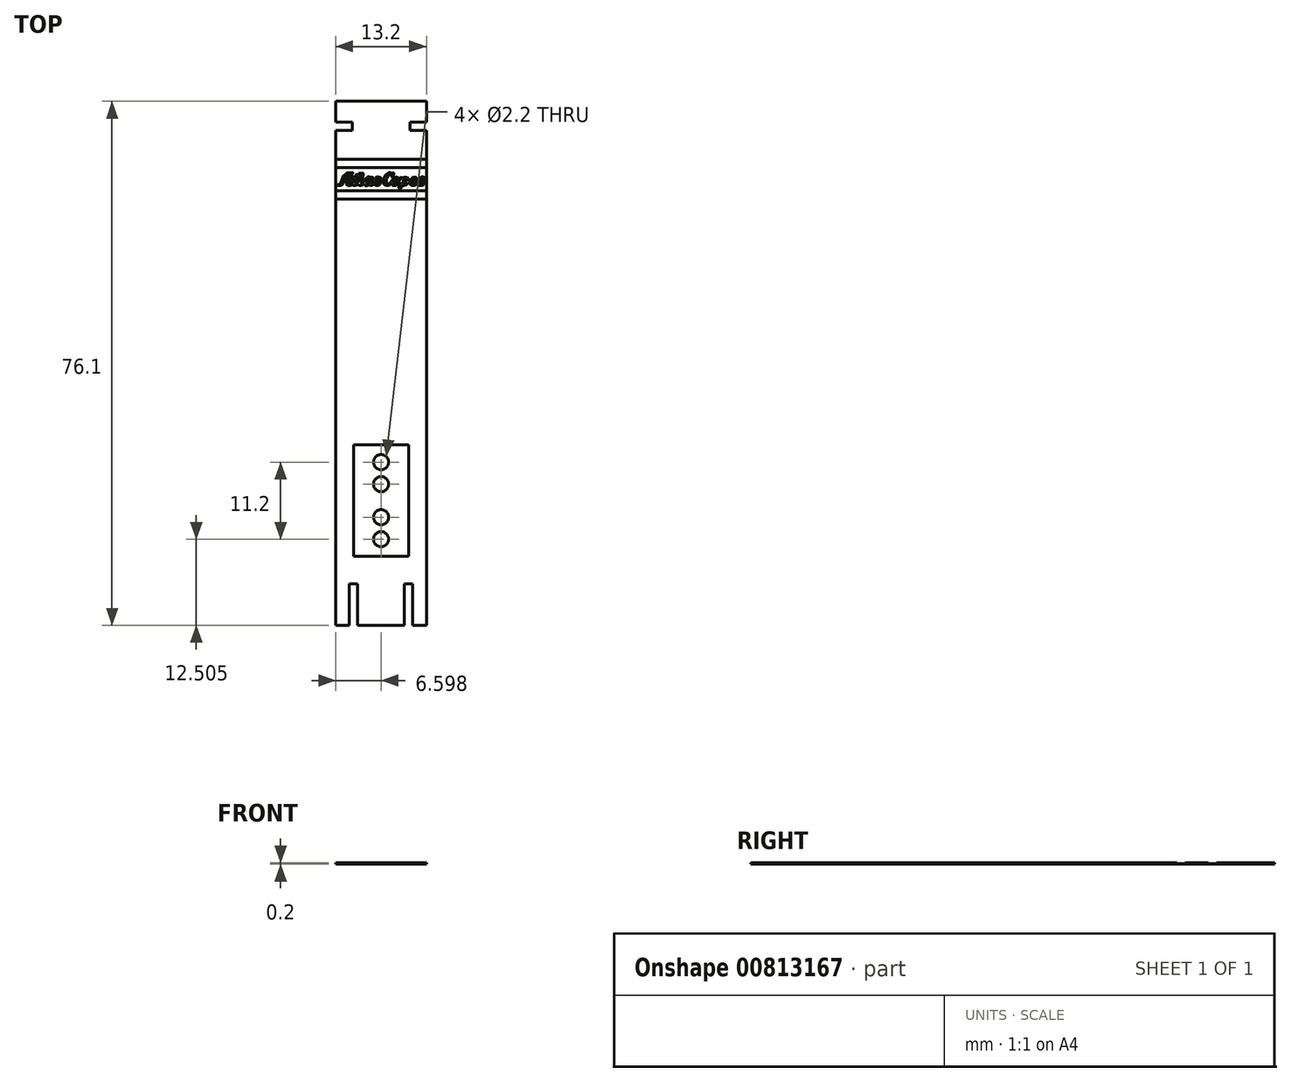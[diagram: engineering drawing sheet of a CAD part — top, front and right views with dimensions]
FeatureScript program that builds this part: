
annotation { "Feature Type Name" : "Feature", "Feature Type Description" : "" }
export const myFeature = defineFeature(function(context is Context, id is Id, definition is map)
    precondition{}
    {
        {
            var Q0;
            Q0=qCreatedBy(makeId("Top.planeOp"),FACE);
            var sketch = newSketch(context, id + "F0", { "sketchPlane" : qUnion([Q0])});
            skLineSegment(sketch, "E0.bottom", {"start": v(-6.48, 59.58) * mm, "end": v(6.72, 59.58) * mm});
            skLineSegment(sketch, "E0.top", {"start": v(-6.48, -16.52) * mm, "end": v(6.72, -16.52) * mm});
            skLineSegment(sketch, "E0.left", {"start": v(-6.48, 59.58) * mm, "end": v(-6.48, -16.52) * mm});
            skLineSegment(sketch, "E0.right", {"start": v(6.72, 59.58) * mm, "end": v(6.72, -16.52) * mm});
            skSolve(sketch);
        }
        {
            var Q0;
            Q0=makeQuery(id+"F0.imprint","IMPRINT",FACE,{"disambiguationData":[TD([[makeQuery(id+"F0.imprint","IMPRINT",EDGE,{"derivedFrom":sQuery(id+"F0.wireOp",EDGE,"E0.bottom")}),-1.0]])]});
            extrude(context, id + "F1", {"entities" : qUnion([Q0]), "depth" : 0.2 * mm, "offsetDistance" : 25 * mm});
        }
        {
            var Q0;
            Q0=makeQuery(id+"F1.opExtrude","CAP_FACE",FACE,{"disambiguationData":[OSD([sQuery(id+"F0.wireOp",EDGE,"E0.bottom"),sQuery(id+"F0.wireOp",EDGE,"E0.top"),sQuery(id+"F0.wireOp",EDGE,"E0.left"),sQuery(id+"F0.wireOp",EDGE,"E0.right")])],"isStart":false});
            var sketch = newSketch(context, id + "F2", { "sketchPlane" : qUnion([Q0])});
            skLineSegment(sketch, "E1", {"start": v(6.72, 56.58) * mm, "end": v(4.32, 56.58) * mm});
            skLineSegment(sketch, "E2", {"start": v(4.32, 56.58) * mm, "end": v(4.32, 55.38) * mm});
            skLineSegment(sketch, "E3", {"start": v(4.32, 55.38) * mm, "end": v(6.72, 55.38) * mm});
            skLineSegment(sketch, "E4", {"start": v(6.72, 55.38) * mm, "end": v(6.72, 56.58) * mm});
            skLineSegment(sketch, "E5", {"start": v(-6.48, 56.58) * mm, "end": v(-4.08, 56.58) * mm});
            skLineSegment(sketch, "E6", {"start": v(-4.08, 56.58) * mm, "end": v(-4.08, 55.38) * mm});
            skLineSegment(sketch, "E7", {"start": v(-4.08, 55.38) * mm, "end": v(-6.48, 55.38) * mm});
            skLineSegment(sketch, "E8", {"start": v(-6.48, 55.38) * mm, "end": v(-6.48, 56.58) * mm});
            skSolve(sketch);
        }
        {
            var Q0;
            Q0=makeQuery(id+"F2.imprint","IMPRINT",FACE,{"disambiguationData":[TD([[makeQuery(id+"F2.imprint","IMPRINT",EDGE,{"derivedFrom":sQuery(id+"F2.wireOp",EDGE,"E5")}),-1.0]])]});
            var Q1;
            Q1=makeQuery(id+"F2.imprint","IMPRINT",FACE,{"disambiguationData":[TD([[makeQuery(id+"F2.imprint","IMPRINT",EDGE,{"derivedFrom":sQuery(id+"F2.wireOp",EDGE,"E1")}),1.0]])]});
            extrude(context, id + "F3", {"entities" : qUnion([Q0, Q1]), "operationType" : NewBodyOperationType.REMOVE, "oppositeDirection" : true, "depth" : 0.2 * mm, "offsetDistance" : 25 * mm});
        }
        {
            var Q0;
            Q0=makeQuery(id+"F1.opExtrude","CAP_FACE",FACE,{"disambiguationData":[OSD([sQuery(id+"F0.wireOp",EDGE,"E0.bottom"),sQuery(id+"F0.wireOp",EDGE,"E0.top"),sQuery(id+"F0.wireOp",EDGE,"E0.left"),sQuery(id+"F0.wireOp",EDGE,"E0.right")])],"isStart":false});
            var sketch = newSketch(context, id + "F4", { "sketchPlane" : qUnion([Q0])});
            skLineSegment(sketch, "E9", {"start": v(6.72, 51.18) * mm, "end": v(-6.48, 51.18) * mm});
            skLineSegment(sketch, "E10", {"start": v(-6.48, 51.18) * mm, "end": v(-6.48, 49.98) * mm});
            skLineSegment(sketch, "E11", {"start": v(-6.48, 49.98) * mm, "end": v(6.72, 49.98) * mm});
            skLineSegment(sketch, "E12", {"start": v(6.72, 49.98) * mm, "end": v(6.72, 51.18) * mm});
            skLineSegment(sketch, "E13", {"start": v(6.72, 46.58) * mm, "end": v(-6.48, 46.58) * mm});
            skLineSegment(sketch, "E14", {"start": v(-6.48, 46.58) * mm, "end": v(-6.48, 45.38) * mm});
            skLineSegment(sketch, "E15", {"start": v(-6.48, 45.38) * mm, "end": v(6.72, 45.38) * mm});
            skLineSegment(sketch, "E16", {"start": v(6.72, 45.38) * mm, "end": v(6.72, 46.58) * mm});
            skSolve(sketch);
        }
        {
            var Q0;
            Q0=makeQuery(id+"F4.imprint","IMPRINT",FACE,{"disambiguationData":[TD([[makeQuery(id+"F4.imprint","IMPRINT",EDGE,{"derivedFrom":sQuery(id+"F4.wireOp",EDGE,"E9")}),1.0]])]});
            var Q1;
            Q1=makeQuery(id+"F4.imprint","IMPRINT",FACE,{"disambiguationData":[TD([[makeQuery(id+"F4.imprint","IMPRINT",EDGE,{"derivedFrom":sQuery(id+"F4.wireOp",EDGE,"E13")}),1.0]])]});
            extrude(context, id + "F5", {"entities" : qUnion([Q0, Q1]), "operationType" : NewBodyOperationType.REMOVE, "oppositeDirection" : true, "depth" : 0.1 * mm, "offsetDistance" : 25 * mm});
        }
        {
            var Q0;
            {var subQ0=sQuery(id+"F0.wireOp",EDGE,"E0.left");var subQ1=sQuery(id+"F0.wireOp",EDGE,"E0.right");Q0=makeQuery(id+"F5.boolean.opBoolean","SPLIT",FACE,{"disambiguationData":[TD([makeQuery(id+"F5.opExtrude","SWEPT_FACE",FACE,{"disambiguationData":[OSD([sQuery(id+"F4.wireOp",EDGE,"E11")])]})])],"derivedFrom":makeQuery(id+"F1.opExtrude","CAP_FACE",FACE,{"disambiguationData":[OSD([sQuery(id+"F0.wireOp",EDGE,"E0.bottom"),sQuery(id+"F0.wireOp",EDGE,"E0.top"),subQ0,subQ1])],"isStart":false})});}
            var sketch = newSketch(context, id + "F6", { "sketchPlane" : qUnion([Q0])});
            skFitSpline(sketch, "E17", {"points": [v(-6.24, 47.53) * mm, v(-6.25, 47.34) * mm, v(-6.22, 47.33) * mm, v(-6.17, 47.33) * mm, v(-6.12, 47.32) * mm, v(-6.08, 47.32) * mm, v(-6.04, 47.33) * mm, v(-6, 47.32) * mm, v(-5.96, 47.33) * mm, v(-5.92, 47.33) * mm, v(-5.88, 47.34) * mm, v(-5.83, 47.35) * mm, v(-5.78, 47.36) * mm, v(-5.55, 47.5) * mm, v(-5.38, 47.67) * mm, v(-5.3, 47.83) * mm, v(-5.25, 47.98) * mm, v(-5.23, 48.04) * mm, v(-5.23, 48.05) * mm, v(-5.22, 48.07) * mm, v(-5.22, 48.1) * mm, v(-5.2, 48.13) * mm, v(-5.18, 48.16) * mm, v(-5.12, 48.17) * mm, v(-5.04, 48.17) * mm, v(-4.97, 48.17) * mm, v(-4.93, 48.17) * mm, v(-4.88, 48.17) * mm, v(-4.85, 48.17) * mm, v(-4.82, 48.17) * mm, v(-4.8, 48.17) * mm, v(-4.8, 48.17) * mm, v(-4.8, 48.13) * mm, v(-4.8, 48.1) * mm, v(-4.81, 48.03) * mm, v(-4.83, 47.97) * mm, v(-4.85, 47.91) * mm, v(-4.86, 47.87) * mm, v(-4.88, 47.81) * mm, v(-4.9, 47.75) * mm, v(-4.92, 47.7) * mm, v(-4.92, 47.55) * mm, v(-4.87, 47.44) * mm, v(-4.78, 47.36) * mm, v(-4.67, 47.32) * mm, v(-4.52, 47.32) * mm, v(-4.41, 47.33) * mm, v(-4.3, 47.37) * mm, v(-4.2, 47.43) * mm, v(-4.13, 47.48) * mm, v(-4.1, 47.51) * mm, v(-4.07, 47.55) * mm, v(-4.05, 47.56) * mm, v(-4.03, 47.52) * mm, v(-4.02, 47.46) * mm, v(-4.01, 47.42) * mm, v(-3.97, 47.4) * mm, v(-3.94, 47.36) * mm, v(-3.89, 47.34) * mm, v(-3.85, 47.33) * mm, v(-3.8, 47.32) * mm], "startDerivative": vector(-1.04, -8.47) * mm, "endDerivative": vector(3.3, -0.6) * mm});
            skFitSpline(sketch, "E18", {"points": [v(-3.8, 47.32) * mm, v(-3.7, 47.32) * mm, v(-3.55, 47.35) * mm, v(-3.45, 47.4) * mm, v(-3.4, 47.43) * mm, v(-3.34, 47.47) * mm, v(-3.3, 47.5) * mm, v(-3.27, 47.53) * mm, v(-3.24, 47.55) * mm, v(-3.2, 47.57) * mm, v(-3.18, 47.56) * mm, v(-3.17, 47.52) * mm, v(-3.14, 47.47) * mm, v(-3.13, 47.42) * mm, v(-3.1, 47.4) * mm, v(-3.06, 47.35) * mm, v(-3, 47.32) * mm, v(-2.94, 47.32) * mm, v(-2.89, 47.32) * mm, v(-2.84, 47.32) * mm, v(-2.8, 47.32) * mm, v(-2.75, 47.32) * mm, v(-2.72, 47.35) * mm, v(-2.69, 47.38) * mm, v(-2.64, 47.4) * mm, v(-2.61, 47.43) * mm, v(-2.58, 47.46) * mm, v(-2.44, 47.57) * mm, v(-2.41, 47.62) * mm, v(-2.39, 47.63) * mm, v(-2.34, 47.63) * mm, v(-2.34, 47.61) * mm, v(-2.34, 47.58) * mm, v(-2.33, 47.56) * mm, v(-2.32, 47.53) * mm, v(-2.25, 47.45) * mm, v(-2.17, 47.38) * mm, v(-2.13, 47.35) * mm, v(-2.06, 47.32) * mm, v(-1.98, 47.32) * mm, v(-1.92, 47.32) * mm, v(-1.83, 47.35) * mm, v(-1.75, 47.4) * mm, v(-1.7, 47.44) * mm, v(-1.66, 47.46) * mm, v(-1.64, 47.48) * mm, v(-1.62, 47.48) * mm, v(-1.6, 47.5) * mm, v(-1.6, 47.48) * mm, v(-1.59, 47.48) * mm, v(-1.57, 47.44) * mm, v(-1.55, 47.42) * mm, v(-1.52, 47.38) * mm, v(-1.5, 47.37) * mm, v(-1.48, 47.36) * mm, v(-1.45, 47.35) * mm], "startDerivative": vector(3.88, -0.24) * mm, "endDerivative": vector(2.21, -0.04) * mm});
            skFitSpline(sketch, "E19", {"points": [v(-1.45, 47.35) * mm, v(-1.4, 47.34) * mm, v(-1.35, 47.34) * mm, v(-1.29, 47.34) * mm, v(-1.22, 47.35) * mm, v(-1.17, 47.37) * mm, v(-1.13, 47.4) * mm, v(-1.1, 47.4) * mm, v(-1.07, 47.42) * mm, v(-1.03, 47.44) * mm, v(-1, 47.47) * mm, v(-0.98, 47.5) * mm, v(-0.97, 47.52) * mm, v(-0.95, 47.53) * mm, v(-0.93, 47.54) * mm, v(-0.9, 47.52) * mm, v(-0.88, 47.49) * mm, v(-0.84, 47.46) * mm, v(-0.8, 47.42) * mm, v(-0.77, 47.39) * mm, v(-0.71, 47.35) * mm, v(-0.67, 47.34) * mm, v(-0.6, 47.32) * mm, v(-0.53, 47.33) * mm, v(-0.47, 47.33) * mm, v(-0.4, 47.33) * mm, v(-0.34, 47.33) * mm, v(-0.3, 47.34) * mm, v(-0.23, 47.37) * mm, v(-0.16, 47.4) * mm, v(-0.13, 47.42) * mm, v(-0.05, 47.48) * mm, v(0.04, 47.6) * mm, v(0.07, 47.73) * mm, v(0.04, 47.89) * mm, v(-0.04, 47.98) * mm, v(-0.16, 48.06) * mm, v(-0.3, 48.14) * mm, v(-0.37, 48.22) * mm, v(-0.4, 48.27) * mm, v(-0.4, 48.34) * mm, v(-0.34, 48.43) * mm, v(-0.3, 48.45) * mm, v(-0.23, 48.46) * mm, v(-0.16, 48.45) * mm, v(-0.14, 48.44) * mm, v(-0.14, 48.39) * mm, v(-0.17, 48.37) * mm, v(-0.18, 48.33) * mm, v(-0.18, 48.3) * mm, v(-0.15, 48.25) * mm, v(-0.13, 48.21) * mm, v(-0.07, 48.17) * mm, v(0, 48.16) * mm, v(0.03, 48.17) * mm, v(0.1, 48.2) * mm, v(0.13, 48.24) * mm, v(0.15, 48.3) * mm, v(0.11, 48.43) * mm, v(0.05, 48.53) * mm, v(-0.04, 48.59) * mm, v(-0.15, 48.63) * mm, v(-0.27, 48.64) * mm, v(-0.4, 48.62) * mm, v(-0.48, 48.6) * mm, v(-0.57, 48.54) * mm, v(-0.66, 48.45) * mm, v(-0.72, 48.36) * mm, v(-0.74, 48.27) * mm, v(-0.74, 48.18) * mm, v(-0.73, 48.08) * mm, v(-0.65, 47.98) * mm, v(-0.6, 47.94) * mm, v(-0.52, 47.88) * mm, v(-0.44, 47.82) * mm, v(-0.37, 47.77) * mm, v(-0.35, 47.68) * mm, v(-0.35, 47.6) * mm, v(-0.39, 47.56) * mm, v(-0.42, 47.53) * mm, v(-0.47, 47.5) * mm, v(-0.5, 47.49) * mm, v(-0.57, 47.46) * mm, v(-0.63, 47.49) * mm, v(-0.68, 47.5) * mm, v(-0.72, 47.55) * mm, v(-0.75, 47.57) * mm, v(-0.76, 47.6) * mm, v(-0.73, 47.63) * mm, v(-0.68, 47.66) * mm, v(-0.65, 47.76) * mm, v(-0.66, 47.84) * mm, v(-0.72, 47.9) * mm, v(-0.8, 47.9) * mm, v(-0.89, 47.9) * mm, v(-0.92, 47.85) * mm, v(-0.96, 47.82) * mm, v(-0.95, 47.74) * mm, v(-0.96, 47.68) * mm, v(-1.01, 47.63) * mm, v(-1.05, 47.6) * mm, v(-1.1, 47.6) * mm], "startDerivative": vector(4.9, -2.39) * mm, "endDerivative": vector(-5.28, -0.79) * mm});
            skFitSpline(sketch, "E20", {"points": [v(-1.1, 47.6) * mm, v(-1.15, 47.6) * mm, v(-1.2, 47.6) * mm, v(-1.22, 47.63) * mm, v(-1.21, 47.72) * mm, v(-1.18, 47.85) * mm, v(-1.14, 48.04) * mm, v(-1.1, 48.25) * mm, v(-1.06, 48.34) * mm, v(-1.04, 48.43) * mm, v(-1.02, 48.52) * mm, v(-1, 48.57) * mm, v(-1.07, 48.58) * mm, v(-1.14, 48.58) * mm, v(-1.22, 48.58) * mm, v(-1.33, 48.58) * mm, v(-1.38, 48.58) * mm, v(-1.38, 48.5) * mm, v(-1.38, 48.5) * mm, v(-1.42, 48.5) * mm, v(-1.45, 48.54) * mm, v(-1.49, 48.56) * mm, v(-1.55, 48.6) * mm, v(-1.63, 48.62) * mm, v(-1.7, 48.63) * mm, v(-1.75, 48.61) * mm, v(-1.81, 48.6) * mm, v(-1.87, 48.57) * mm, v(-1.91, 48.54) * mm, v(-1.96, 48.5) * mm, v(-2.05, 48.44) * mm, v(-2.13, 48.34) * mm, v(-2.2, 48.26) * mm, v(-2.25, 48.2) * mm, v(-2.28, 48.13) * mm, v(-2.37, 47.98) * mm, v(-2.4, 47.9) * mm, v(-2.44, 47.86) * mm, v(-2.47, 47.8) * mm, v(-2.52, 47.73) * mm, v(-2.6, 47.65) * mm, v(-2.61, 47.62) * mm, v(-2.64, 47.6) * mm, v(-2.67, 47.6) * mm, v(-2.7, 47.6) * mm, v(-2.71, 47.61) * mm, v(-2.73, 47.62) * mm, v(-2.75, 47.63) * mm, v(-2.75, 47.64) * mm, v(-2.76, 47.66) * mm, v(-2.75, 47.72) * mm, v(-2.73, 47.8) * mm, v(-2.71, 47.89) * mm, v(-2.69, 47.97) * mm, v(-2.65, 48.1) * mm, v(-2.63, 48.18) * mm, v(-2.61, 48.32) * mm, v(-2.58, 48.48) * mm, v(-2.53, 48.65) * mm, v(-2.49, 48.77) * mm, v(-2.45, 48.9) * mm, v(-2.43, 49) * mm, v(-2.42, 49.1) * mm, v(-2.42, 49.13) * mm, v(-2.44, 49.14) * mm, v(-2.48, 49.13) * mm, v(-2.5, 49.13) * mm, v(-2.68, 49.14) * mm, v(-2.78, 49.14) * mm, v(-2.92, 49.14) * mm, v(-3.03, 49.15) * mm, v(-3.07, 49.15) * mm, v(-3.07, 49.12) * mm, v(-3.08, 49.05) * mm, v(-3.09, 49) * mm, v(-3.07, 48.97) * mm, v(-3.03, 48.96) * mm, v(-2.97, 48.97) * mm, v(-2.93, 48.97) * mm, v(-2.89, 48.97) * mm, v(-2.87, 48.97) * mm, v(-2.88, 48.9) * mm, v(-2.9, 48.81) * mm, v(-2.9, 48.75) * mm, v(-2.93, 48.65) * mm], "startDerivative": vector(-5.04, 0.24) * mm, "endDerivative": vector(-1.95, -7.23) * mm});
            skFitSpline(sketch, "E21", {"points": [v(-2.93, 48.65) * mm, v(-2.96, 48.52) * mm, v(-2.97, 48.43) * mm, v(-3, 48.3) * mm, v(-3.02, 48.23) * mm, v(-3.05, 48.16) * mm, v(-3.07, 48.06) * mm, v(-3.1, 48) * mm, v(-3.13, 47.9) * mm, v(-3.17, 47.82) * mm, v(-3.23, 47.76) * mm, v(-3.28, 47.7) * mm, v(-3.35, 47.66) * mm, v(-3.41, 47.63) * mm, v(-3.45, 47.6) * mm, v(-3.5, 47.6) * mm, v(-3.55, 47.6) * mm, v(-3.6, 47.61) * mm, v(-3.62, 47.62) * mm, v(-3.64, 47.67) * mm, v(-3.63, 47.75) * mm, v(-3.62, 47.84) * mm, v(-3.6, 47.93) * mm, v(-3.57, 48.08) * mm, v(-3.53, 48.22) * mm, v(-3.51, 48.32) * mm, v(-3.5, 48.4) * mm, v(-3.48, 48.44) * mm, v(-3.42, 48.44) * mm, v(-3.3, 48.44) * mm, v(-3.2, 48.44) * mm, v(-3.19, 48.44) * mm, v(-3.18, 48.48) * mm, v(-3.18, 48.54) * mm, v(-3.18, 48.57) * mm, v(-3.23, 48.57) * mm, v(-3.3, 48.57) * mm, v(-3.39, 48.56) * mm, v(-3.42, 48.57) * mm, v(-3.43, 48.62) * mm, v(-3.41, 48.65) * mm, v(-3.4, 48.7) * mm, v(-3.38, 48.75) * mm, v(-3.36, 48.84) * mm, v(-3.35, 48.9) * mm, v(-3.34, 48.95) * mm, v(-3.34, 48.96) * mm, v(-3.4, 48.97) * mm, v(-3.42, 48.97) * mm, v(-3.49, 48.98) * mm, v(-3.5, 48.96) * mm, v(-3.5, 48.93) * mm, v(-3.55, 48.88) * mm, v(-3.56, 48.85) * mm, v(-3.58, 48.8) * mm, v(-3.62, 48.77) * mm, v(-3.64, 48.75) * mm, v(-3.67, 48.72) * mm, v(-3.7, 48.69) * mm, v(-3.71, 48.68) * mm, v(-3.75, 48.65) * mm, v(-3.79, 48.61) * mm, v(-3.82, 48.59) * mm, v(-3.88, 48.59) * mm, v(-3.92, 48.59) * mm, v(-3.96, 48.59) * mm, v(-4.01, 48.59) * mm, v(-4.05, 48.59) * mm, v(-4.07, 48.53) * mm, v(-4.06, 48.5) * mm, v(-4.08, 48.44) * mm, v(-4.05, 48.43) * mm, v(-4.02, 48.43) * mm, v(-3.98, 48.43) * mm, v(-3.95, 48.44) * mm, v(-3.9, 48.43) * mm, v(-3.88, 48.43) * mm, v(-3.86, 48.43) * mm, v(-3.87, 48.4) * mm, v(-3.88, 48.37) * mm, v(-3.89, 48.34) * mm, v(-3.9, 48.29) * mm, v(-3.92, 48.23) * mm, v(-3.92, 48.18) * mm, v(-3.94, 48.13) * mm, v(-3.96, 48.07) * mm, v(-3.98, 48) * mm, v(-4.01, 47.93) * mm, v(-4.04, 47.86) * mm, v(-4.07, 47.8) * mm, v(-4.1, 47.74) * mm, v(-4.15, 47.68) * mm, v(-4.2, 47.64) * mm, v(-4.25, 47.6) * mm, v(-4.28, 47.58) * mm, v(-4.31, 47.56) * mm, v(-4.38, 47.55) * mm, v(-4.47, 47.56) * mm, v(-4.5, 47.6) * mm, v(-4.5, 47.67) * mm, v(-4.48, 47.8) * mm, v(-4.46, 47.91) * mm, v(-4.42, 48.07) * mm, v(-4.37, 48.21) * mm, v(-4.36, 48.25) * mm, v(-4.32, 48.38) * mm, v(-4.3, 48.49) * mm, v(-4.26, 48.59) * mm, v(-4.25, 48.67) * mm, v(-4.21, 48.78) * mm, v(-4.21, 48.8) * mm, v(-4.2, 48.88) * mm, v(-4.17, 49) * mm, v(-4.15, 49.06) * mm, v(-4.14, 49.08) * mm, v(-4.1, 49.08) * mm, v(-4.07, 49.08) * mm, v(-4.03, 49.08) * mm, v(-3.97, 49.09) * mm, v(-3.92, 49.09) * mm, v(-3.9, 49.09) * mm, v(-3.87, 49.1) * mm, v(-3.87, 49.15) * mm, v(-3.86, 49.18) * mm, v(-3.86, 49.2) * mm, v(-3.86, 49.2) * mm, v(-3.9, 49.22) * mm, v(-3.96, 49.22) * mm, v(-4.03, 49.22) * mm, v(-4.07, 49.22) * mm, v(-4.12, 49.23) * mm, v(-4.2, 49.22) * mm, v(-4.27, 49.22) * mm, v(-4.32, 49.2) * mm, v(-4.4, 49.21) * mm, v(-4.45, 49.2) * mm, v(-4.5, 49.21) * mm, v(-4.53, 49.21) * mm, v(-4.58, 49.2) * mm, v(-4.72, 49.2) * mm, v(-4.79, 49.18) * mm, v(-4.88, 49.14) * mm, v(-4.97, 49.1) * mm, v(-5.1, 49.02) * mm, v(-5.2, 48.95) * mm, v(-5.29, 48.85) * mm, v(-5.38, 48.72) * mm, v(-5.49, 48.54) * mm, v(-5.54, 48.4) * mm, v(-5.6, 48.22) * mm, v(-5.63, 48.08) * mm, v(-5.68, 47.93) * mm, v(-5.71, 47.78) * mm, v(-5.76, 47.64) * mm, v(-5.8, 47.6) * mm, v(-5.87, 47.55) * mm, v(-5.92, 47.52) * mm, v(-5.96, 47.49) * mm, v(-5.98, 47.48) * mm, v(-6.05, 47.48) * mm, v(-6.1, 47.47) * mm, v(-6.15, 47.47) * mm, v(-6.18, 47.47) * mm, v(-6.2, 47.5) * mm, v(-6.22, 47.5) * mm, v(-6.23, 47.52) * mm, v(-6.24, 47.53) * mm, v(-6.25, 47.51) * mm], "startDerivative": vector(-4.15, -15.73) * mm, "endDerivative": vector(0.75, -6.6) * mm});
            skFitSpline(sketch, "E22", {"points": [v(-5.14, 48.3) * mm, v(-5.02, 48.3) * mm, v(-4.96, 48.29) * mm, v(-4.87, 48.29) * mm, v(-4.8, 48.28) * mm, v(-4.76, 48.29) * mm, v(-4.74, 48.33) * mm, v(-4.71, 48.38) * mm, v(-4.7, 48.45) * mm, v(-4.68, 48.53) * mm, v(-4.64, 48.63) * mm, v(-4.62, 48.7) * mm, v(-4.6, 48.77) * mm, v(-4.58, 48.86) * mm, v(-4.56, 48.93) * mm, v(-4.54, 48.98) * mm, v(-4.53, 49.02) * mm, v(-4.53, 49.04) * mm, v(-4.54, 49.05) * mm, v(-4.58, 49.06) * mm, v(-4.6, 49.06) * mm, v(-4.63, 49.06) * mm, v(-4.67, 49.06) * mm, v(-4.7, 49.05) * mm, v(-4.74, 49.05) * mm, v(-4.78, 49) * mm, v(-4.81, 48.99) * mm, v(-4.84, 48.95) * mm, v(-4.86, 48.94) * mm, v(-4.88, 48.9) * mm, v(-4.9, 48.89) * mm, v(-4.93, 48.85) * mm, v(-4.96, 48.82) * mm, v(-4.97, 48.8) * mm, v(-5, 48.76) * mm, v(-5.01, 48.74) * mm, v(-5.03, 48.71) * mm, v(-5.04, 48.68) * mm, v(-5.07, 48.65) * mm, v(-5.08, 48.59) * mm, v(-5.1, 48.53) * mm, v(-5.12, 48.5) * mm, v(-5.13, 48.45) * mm, v(-5.14, 48.41) * mm, v(-5.15, 48.38) * mm, v(-5.16, 48.34) * mm, v(-5.16, 48.32) * mm, v(-5.14, 48.3) * mm]});
            skFitSpline(sketch, "E23", {"points": [v(-1.62, 48.42) * mm, v(-1.68, 48.42) * mm, v(-1.71, 48.4) * mm, v(-1.74, 48.4) * mm, v(-1.77, 48.36) * mm, v(-1.8, 48.32) * mm, v(-1.83, 48.28) * mm, v(-1.84, 48.24) * mm, v(-1.87, 48.2) * mm, v(-1.88, 48.16) * mm, v(-1.9, 48.13) * mm, v(-1.93, 48.05) * mm, v(-1.94, 48.02) * mm, v(-1.95, 47.98) * mm, v(-1.96, 47.9) * mm, v(-1.96, 47.83) * mm, v(-1.96, 47.77) * mm, v(-1.96, 47.71) * mm, v(-1.94, 47.64) * mm, v(-1.92, 47.6) * mm, v(-1.88, 47.6) * mm, v(-1.87, 47.6) * mm, v(-1.84, 47.58) * mm, v(-1.82, 47.57) * mm, v(-1.8, 47.57) * mm, v(-1.79, 47.57) * mm, v(-1.76, 47.58) * mm, v(-1.74, 47.6) * mm, v(-1.7, 47.6) * mm, v(-1.69, 47.63) * mm, v(-1.67, 47.64) * mm, v(-1.66, 47.66) * mm, v(-1.65, 47.67) * mm, v(-1.64, 47.69) * mm, v(-1.64, 47.7) * mm, v(-1.63, 47.71) * mm, v(-1.62, 47.74) * mm, v(-1.6, 47.75) * mm, v(-1.59, 47.78) * mm, v(-1.58, 47.8) * mm, v(-1.57, 47.87) * mm, v(-1.55, 47.9) * mm, v(-1.55, 47.92) * mm, v(-1.55, 47.95) * mm, v(-1.53, 47.98) * mm, v(-1.53, 48) * mm, v(-1.53, 48.02) * mm, v(-1.52, 48.05) * mm, v(-1.51, 48.07) * mm, v(-1.51, 48.09) * mm, v(-1.51, 48.13) * mm, v(-1.5, 48.2) * mm, v(-1.5, 48.26) * mm, v(-1.5, 48.3) * mm, v(-1.5, 48.34) * mm, v(-1.51, 48.36) * mm, v(-1.52, 48.4) * mm, v(-1.52, 48.4) * mm, v(-1.56, 48.41) * mm, v(-1.6, 48.43) * mm, v(-1.62, 48.42) * mm]});
            skFitSpline(sketch, "E24", {"points": [v(1.18, 49.19) * mm, v(1.1, 49.13) * mm, v(1, 49.08) * mm, v(0.86, 48.96) * mm, v(0.75, 48.82) * mm, v(0.66, 48.7) * mm, v(0.6, 48.6) * mm, v(0.56, 48.54) * mm, v(0.54, 48.47) * mm, v(0.5, 48.37) * mm, v(0.47, 48.23) * mm, v(0.46, 48.07) * mm, v(0.44, 48) * mm, v(0.45, 47.9) * mm, v(0.46, 47.77) * mm, v(0.5, 47.67) * mm, v(0.54, 47.56) * mm, v(0.62, 47.49) * mm, v(0.75, 47.4) * mm, v(0.86, 47.35) * mm, v(0.98, 47.35) * mm, v(1.07, 47.33) * mm, v(1.14, 47.35) * mm, v(1.23, 47.4) * mm, v(1.32, 47.44) * mm, v(1.37, 47.47) * mm, v(1.4, 47.5) * mm, v(1.45, 47.53) * mm, v(1.5, 47.58) * mm, v(1.53, 47.6) * mm, v(1.55, 47.63) * mm, v(1.58, 47.66) * mm, v(1.58, 47.66) * mm, v(1.62, 47.6) * mm, v(1.66, 47.5) * mm, v(1.67, 47.47) * mm, v(1.68, 47.46) * mm, v(1.7, 47.44) * mm, v(1.73, 47.4) * mm, v(1.74, 47.4) * mm, v(1.77, 47.38) * mm, v(1.8, 47.37) * mm, v(1.83, 47.36) * mm, v(1.87, 47.35) * mm, v(1.9, 47.35) * mm, v(1.96, 47.34) * mm, v(2.02, 47.33) * mm, v(2.06, 47.33) * mm, v(2.13, 47.34) * mm, v(2.19, 47.34) * mm, v(2.23, 47.35) * mm, v(2.3, 47.38) * mm, v(2.4, 47.44) * mm, v(2.47, 47.5) * mm, v(2.53, 47.53) * mm, v(2.6, 47.6) * mm, v(2.63, 47.63) * mm, v(2.68, 47.66) * mm, v(2.74, 47.72) * mm], "startDerivative": vector(-4.33, -2.8) * mm, "endDerivative": vector(3.64, 3.4) * mm});
            skFitSpline(sketch, "E25", {"points": [v(2.74, 47.72) * mm, v(2.8, 47.78) * mm, v(2.85, 47.83) * mm, v(2.9, 47.87) * mm, v(2.9, 47.82) * mm, v(2.9, 47.77) * mm, v(2.89, 47.75) * mm, v(2.88, 47.72) * mm, v(2.87, 47.65) * mm, v(2.84, 47.53) * mm, v(2.8, 47.44) * mm, v(2.79, 47.4) * mm, v(2.78, 47.33) * mm, v(2.77, 47.28) * mm, v(2.74, 47.17) * mm, v(2.71, 47.09) * mm, v(2.7, 47.04) * mm, v(2.68, 46.99) * mm, v(2.68, 46.96) * mm, v(2.69, 46.94) * mm, v(2.72, 46.92) * mm, v(2.74, 46.92) * mm, v(2.83, 46.92) * mm, v(2.89, 46.92) * mm, v(2.97, 46.91) * mm, v(3, 46.91) * mm, v(3.05, 46.9) * mm, v(3.1, 46.95) * mm, v(3.1, 47) * mm, v(3.1, 47.03) * mm, v(3.1, 47.08) * mm, v(3.12, 47.15) * mm, v(3.14, 47.21) * mm, v(3.16, 47.28) * mm, v(3.16, 47.34) * mm, v(3.18, 47.38) * mm, v(3.18, 47.43) * mm, v(3.2, 47.44) * mm, v(3.22, 47.42) * mm, v(3.23, 47.41) * mm, v(3.28, 47.38) * mm, v(3.3, 47.37) * mm, v(3.33, 47.36) * mm, v(3.38, 47.35) * mm, v(3.44, 47.34) * mm, v(3.47, 47.34) * mm, v(3.52, 47.34) * mm, v(3.57, 47.34) * mm, v(3.6, 47.35) * mm, v(3.67, 47.37) * mm, v(3.75, 47.42) * mm, v(3.8, 47.45) * mm, v(3.83, 47.48) * mm, v(3.9, 47.54) * mm, v(4, 47.62) * mm, v(4.08, 47.67) * mm, v(4.11, 47.72) * mm, v(4.16, 47.77) * mm, v(4.18, 47.8) * mm, v(4.23, 47.83) * mm, v(4.24, 47.85) * mm, v(4.3, 47.87) * mm, v(4.32, 47.9) * mm, v(4.33, 47.82) * mm, v(4.32, 47.79) * mm, v(4.32, 47.75) * mm, v(4.32, 47.7) * mm, v(4.33, 47.66) * mm, v(4.33, 47.61) * mm, v(4.34, 47.54) * mm, v(4.36, 47.52) * mm, v(4.38, 47.47) * mm, v(4.45, 47.41) * mm, v(4.47, 47.4) * mm, v(4.52, 47.37) * mm, v(4.53, 47.36) * mm, v(4.58, 47.34) * mm, v(4.64, 47.33) * mm, v(4.68, 47.32) * mm, v(4.79, 47.33) * mm, v(4.85, 47.32) * mm, v(4.9, 47.33) * mm, v(4.94, 47.36) * mm, v(5, 47.38) * mm, v(5.04, 47.41) * mm, v(5.08, 47.44) * mm, v(5.13, 47.47) * mm, v(5.15, 47.5) * mm, v(5.2, 47.55) * mm, v(5.23, 47.58) * mm, v(5.27, 47.61) * mm, v(5.3, 47.66) * mm, v(5.34, 47.7) * mm, v(5.36, 47.72) * mm, v(5.37, 47.72) * mm, v(5.37, 47.72) * mm, v(5.38, 47.72) * mm, v(5.38, 47.7) * mm, v(5.39, 47.68) * mm, v(5.39, 47.65) * mm, v(5.4, 47.63) * mm, v(5.4, 47.6) * mm, v(5.4, 47.58) * mm, v(5.4, 47.56) * mm, v(5.42, 47.55) * mm, v(5.45, 47.52) * mm, v(5.47, 47.49) * mm, v(5.49, 47.46) * mm, v(5.51, 47.45) * mm, v(5.53, 47.42) * mm, v(5.56, 47.4) * mm, v(5.58, 47.38) * mm, v(5.6, 47.37) * mm, v(5.62, 47.36) * mm, v(5.66, 47.36) * mm, v(5.7, 47.35) * mm, v(5.72, 47.35) * mm, v(5.74, 47.35) * mm, v(5.77, 47.35) * mm, v(5.8, 47.34) * mm, v(5.83, 47.34) * mm, v(5.86, 47.34) * mm, v(5.9, 47.34) * mm, v(5.91, 47.34) * mm, v(5.94, 47.34) * mm, v(5.97, 47.34) * mm, v(5.98, 47.34) * mm, v(6, 47.34) * mm, v(6.06, 47.36) * mm, v(6.19, 47.41) * mm, v(6.22, 47.44) * mm, v(6.26, 47.48) * mm, v(6.3, 47.5) * mm, v(6.32, 47.55) * mm, v(6.36, 47.57) * mm, v(6.42, 47.65) * mm, v(6.45, 47.72) * mm, v(6.48, 47.8) * mm, v(6.51, 47.85) * mm, v(6.53, 47.88) * mm, v(6.54, 47.93) * mm, v(6.55, 47.96) * mm, v(6.55, 48.02) * mm, v(6.55, 48.08) * mm, v(6.56, 48.13) * mm, v(6.55, 48.18) * mm, v(6.55, 48.22) * mm, v(6.54, 48.28) * mm, v(6.53, 48.32) * mm, v(6.51, 48.37) * mm, v(6.5, 48.41) * mm, v(6.46, 48.44) * mm, v(6.43, 48.51) * mm, v(6.4, 48.52) * mm, v(6.37, 48.57) * mm, v(6.34, 48.59) * mm], "startDerivative": vector(6.36, 8.36) * mm, "endDerivative": vector(-2.85, 6.84) * mm});
            skFitSpline(sketch, "E26", {"points": [v(6.34, 48.59) * mm, v(6.3, 48.61) * mm, v(6.23, 48.63) * mm, v(6.15, 48.64) * mm, v(6.12, 48.64) * mm, v(6.06, 48.63) * mm, v(6.01, 48.63) * mm, v(5.99, 48.6) * mm, v(5.95, 48.59) * mm, v(5.91, 48.59) * mm, v(5.9, 48.56) * mm, v(5.89, 48.54) * mm, v(5.86, 48.53) * mm, v(5.84, 48.51) * mm, v(5.83, 48.5) * mm, v(5.8, 48.48) * mm, v(5.78, 48.46) * mm, v(5.75, 48.44) * mm, v(5.73, 48.42) * mm, v(5.7, 48.39) * mm, v(5.67, 48.36) * mm, v(5.65, 48.34) * mm, v(5.62, 48.3) * mm, v(5.6, 48.28) * mm, v(5.57, 48.23) * mm, v(5.53, 48.2) * mm, v(5.5, 48.16) * mm, v(5.48, 48.12) * mm, v(5.44, 48.07) * mm, v(5.4, 48.02) * mm, v(5.37, 47.96) * mm, v(5.35, 47.92) * mm, v(5.3, 47.88) * mm, v(5.28, 47.84) * mm, v(5.26, 47.8) * mm, v(5.22, 47.77) * mm, v(5.2, 47.75) * mm, v(5.18, 47.72) * mm, v(5.14, 47.7) * mm, v(5.11, 47.66) * mm, v(5.08, 47.63) * mm, v(5.06, 47.61) * mm, v(5.04, 47.6) * mm, v(5.02, 47.58) * mm, v(5, 47.58) * mm, v(4.98, 47.56) * mm, v(4.96, 47.56) * mm, v(4.92, 47.55) * mm, v(4.86, 47.55) * mm, v(4.85, 47.55) * mm, v(4.8, 47.57) * mm, v(4.78, 47.59) * mm, v(4.78, 47.6) * mm, v(4.74, 47.61) * mm, v(4.73, 47.64) * mm, v(4.72, 47.66) * mm, v(4.71, 47.72) * mm, v(4.71, 47.77) * mm, v(4.7, 47.79) * mm, v(4.71, 47.83) * mm, v(4.72, 47.92) * mm, v(4.72, 47.94) * mm, v(4.73, 48.02) * mm, v(4.73, 48.03) * mm, v(4.74, 48.06) * mm, v(4.76, 48.11) * mm, v(4.77, 48.14) * mm, v(4.8, 48.2) * mm, v(4.82, 48.24) * mm, v(4.84, 48.27) * mm, v(4.86, 48.3) * mm, v(4.89, 48.35) * mm, v(4.9, 48.37) * mm, v(4.93, 48.42) * mm, v(4.96, 48.44) * mm, v(5, 48.46) * mm, v(5.01, 48.47) * mm, v(5.04, 48.48) * mm, v(5.08, 48.49) * mm, v(5.1, 48.48) * mm, v(5.13, 48.47) * mm, v(5.16, 48.46) * mm, v(5.17, 48.45) * mm, v(5.19, 48.42) * mm, v(5.19, 48.4) * mm, v(5.18, 48.39) * mm, v(5.14, 48.37) * mm, v(5.12, 48.37) * mm, v(5.1, 48.36) * mm, v(5.07, 48.36) * mm, v(5.05, 48.33) * mm, v(5.04, 48.3) * mm, v(5.04, 48.25) * mm, v(5.04, 48.22) * mm, v(5.05, 48.17) * mm, v(5.06, 48.15) * mm, v(5.08, 48.12) * mm, v(5.1, 48.1) * mm, v(5.12, 48.1) * mm, v(5.16, 48.09) * mm, v(5.2, 48.09) * mm, v(5.24, 48.1) * mm, v(5.26, 48.1) * mm, v(5.3, 48.13) * mm, v(5.33, 48.16) * mm, v(5.35, 48.18) * mm, v(5.36, 48.2) * mm, v(5.37, 48.25) * mm, v(5.38, 48.31) * mm, v(5.38, 48.34) * mm, v(5.38, 48.37) * mm, v(5.37, 48.4) * mm, v(5.37, 48.43) * mm, v(5.35, 48.46) * mm, v(5.3, 48.5) * mm, v(5.28, 48.53) * mm, v(5.25, 48.56) * mm, v(5.23, 48.58) * mm, v(5.18, 48.59) * mm, v(5.17, 48.61) * mm, v(5.14, 48.62) * mm, v(5.12, 48.62) * mm, v(5.1, 48.62) * mm, v(5.07, 48.62) * mm, v(5.06, 48.62) * mm, v(5.03, 48.63) * mm, v(4.99, 48.62) * mm, v(4.93, 48.61) * mm, v(4.88, 48.59) * mm, v(4.83, 48.59) * mm, v(4.8, 48.58) * mm, v(4.78, 48.55) * mm, v(4.75, 48.54) * mm, v(4.7, 48.51) * mm, v(4.67, 48.48) * mm, v(4.63, 48.44) * mm, v(4.61, 48.4) * mm, v(4.55, 48.35) * mm, v(4.52, 48.32) * mm, v(4.48, 48.27) * mm, v(4.41, 48.18) * mm, v(4.4, 48.17) * mm, v(4.36, 48.14) * mm, v(4.32, 48.1) * mm, v(4.3, 48.07) * mm, v(4.26, 48.05) * mm, v(4.23, 48.01) * mm, v(4.21, 48) * mm, v(4.2, 47.97) * mm, v(4.16, 47.95) * mm, v(4.13, 47.93) * mm, v(4.1, 47.95) * mm, v(4.1, 47.98) * mm, v(4.1, 48.04) * mm, v(4.12, 48.1) * mm, v(4.13, 48.15) * mm, v(4.13, 48.2) * mm, v(4.14, 48.26) * mm, v(4.13, 48.3) * mm, v(4.12, 48.34) * mm, v(4.08, 48.4) * mm, v(4.04, 48.45) * mm, v(4.01, 48.5) * mm, v(3.93, 48.56) * mm, v(3.87, 48.58) * mm, v(3.81, 48.59) * mm, v(3.78, 48.59) * mm, v(3.72, 48.59) * mm, v(3.7, 48.59) * mm, v(3.65, 48.59) * mm, v(3.6, 48.59) * mm, v(3.56, 48.58) * mm, v(3.53, 48.55) * mm, v(3.52, 48.54) * mm, v(3.5, 48.52) * mm, v(3.5, 48.52) * mm, v(3.48, 48.52) * mm, v(3.46, 48.52) * mm, v(3.46, 48.52) * mm, v(3.45, 48.55) * mm, v(3.46, 48.56) * mm, v(3.47, 48.58) * mm, v(3.44, 48.58) * mm, v(3.38, 48.58) * mm, v(3.38, 48.58) * mm, v(3.27, 48.58) * mm, v(3.21, 48.58) * mm, v(3.12, 48.58) * mm, v(3.06, 48.58) * mm, v(2.98, 48.58) * mm, v(2.92, 48.58) * mm, v(2.92, 48.56) * mm, v(2.92, 48.53) * mm, v(2.91, 48.5) * mm, v(2.92, 48.47) * mm, v(2.94, 48.46) * mm, v(2.97, 48.46) * mm, v(3, 48.46) * mm, v(3.02, 48.46) * mm, v(3.04, 48.46) * mm, v(3.05, 48.45) * mm, v(3.05, 48.42) * mm, v(3.04, 48.38) * mm, v(3.03, 48.35) * mm, v(3.01, 48.32) * mm, v(2.98, 48.3) * mm, v(2.97, 48.25) * mm, v(2.94, 48.21) * mm, v(2.92, 48.17) * mm, v(2.91, 48.15) * mm, v(2.9, 48.12) * mm, v(2.86, 48.1) * mm, v(2.85, 48.08) * mm, v(2.83, 48.05) * mm, v(2.81, 48.02) * mm, v(2.79, 48) * mm, v(2.76, 47.97) * mm, v(2.74, 47.95) * mm, v(2.72, 47.94) * mm, v(2.72, 47.95) * mm, v(2.7, 47.97) * mm, v(2.7, 48) * mm, v(2.71, 48.04) * mm, v(2.71, 48.06) * mm, v(2.71, 48.11) * mm, v(2.71, 48.15) * mm, v(2.7, 48.18) * mm, v(2.71, 48.2) * mm, v(2.71, 48.24) * mm, v(2.71, 48.27) * mm, v(2.7, 48.32) * mm, v(2.7, 48.34) * mm, v(2.68, 48.38) * mm, v(2.68, 48.41) * mm, v(2.66, 48.44) * mm, v(2.63, 48.47) * mm, v(2.6, 48.5) * mm, v(2.58, 48.53) * mm, v(2.54, 48.55) * mm, v(2.5, 48.56) * mm, v(2.5, 48.58) * mm, v(2.48, 48.58) * mm, v(2.46, 48.59) * mm, v(2.45, 48.6) * mm, v(2.43, 48.61) * mm, v(2.4, 48.61) * mm, v(2.37, 48.61) * mm, v(2.33, 48.62) * mm, v(2.28, 48.62) * mm, v(2.26, 48.62) * mm, v(2.22, 48.62) * mm, v(2.2, 48.6) * mm, v(2.16, 48.59) * mm, v(2.12, 48.58) * mm, v(2.1, 48.55) * mm, v(2.07, 48.52) * mm, v(2.05, 48.5) * mm, v(2.02, 48.48) * mm, v(1.98, 48.45) * mm, v(1.97, 48.43) * mm, v(1.93, 48.4) * mm, v(1.9, 48.37) * mm, v(1.87, 48.35) * mm, v(1.83, 48.3) * mm, v(1.8, 48.28) * mm, v(1.78, 48.25) * mm, v(1.76, 48.21) * mm, v(1.72, 48.17) * mm, v(1.7, 48.15) * mm, v(1.68, 48.1) * mm, v(1.65, 48.07) * mm, v(1.63, 48.03) * mm, v(1.58, 47.98) * mm, v(1.56, 47.93) * mm, v(1.54, 47.87) * mm, v(1.5, 47.86) * mm, v(1.5, 47.82) * mm, v(1.48, 47.8) * mm, v(1.46, 47.79) * mm, v(1.45, 47.76) * mm, v(1.43, 47.73) * mm, v(1.4, 47.71) * mm, v(1.38, 47.7) * mm, v(1.36, 47.68) * mm, v(1.33, 47.66) * mm, v(1.31, 47.64) * mm, v(1.29, 47.62) * mm, v(1.25, 47.6) * mm, v(1.24, 47.58) * mm, v(1.2, 47.57) * mm, v(1.16, 47.55) * mm, v(1.14, 47.55) * mm, v(1.1, 47.55) * mm, v(1.07, 47.55) * mm, v(1.05, 47.56) * mm, v(1.02, 47.57) * mm, v(0.98, 47.6) * mm, v(0.97, 47.6) * mm, v(0.95, 47.63) * mm, v(0.93, 47.66) * mm, v(0.93, 47.69) * mm, v(0.9, 47.74) * mm, v(0.9, 47.77) * mm], "startDerivative": vector(-10.1, 7.15) * mm, "endDerivative": vector(0.7, 8.18) * mm});
            skFitSpline(sketch, "E27", {"points": [v(0.9, 47.77) * mm, v(0.9, 47.82) * mm, v(0.87, 47.87) * mm, v(0.87, 47.9) * mm, v(0.86, 47.96) * mm, v(0.87, 47.98) * mm, v(0.87, 48.05) * mm, v(0.88, 48.08) * mm, v(0.9, 48.14) * mm, v(0.9, 48.15) * mm, v(0.9, 48.23) * mm, v(0.9, 48.26) * mm, v(0.92, 48.3) * mm, v(0.93, 48.33) * mm, v(0.94, 48.36) * mm, v(0.96, 48.38) * mm, v(0.98, 48.43) * mm, v(1, 48.48) * mm, v(1.02, 48.54) * mm, v(1.04, 48.6) * mm, v(1.09, 48.66) * mm, v(1.12, 48.7) * mm, v(1.14, 48.74) * mm, v(1.17, 48.77) * mm, v(1.2, 48.83) * mm, v(1.24, 48.85) * mm, v(1.26, 48.9) * mm, v(1.3, 48.92) * mm, v(1.33, 48.95) * mm, v(1.36, 48.98) * mm, v(1.39, 49) * mm, v(1.42, 49.01) * mm, v(1.44, 49.02) * mm, v(1.45, 49.02) * mm, v(1.48, 49.02) * mm, v(1.5, 49.02) * mm, v(1.52, 49.01) * mm, v(1.55, 49) * mm, v(1.56, 48.99) * mm, v(1.6, 48.94) * mm, v(1.62, 48.92) * mm, v(1.63, 48.9) * mm, v(1.65, 48.85) * mm, v(1.66, 48.8) * mm, v(1.67, 48.78) * mm, v(1.67, 48.73) * mm, v(1.67, 48.7) * mm, v(1.68, 48.66) * mm, v(1.68, 48.64) * mm, v(1.68, 48.62) * mm, v(1.68, 48.59) * mm, v(1.7, 48.57) * mm, v(1.72, 48.58) * mm, v(1.75, 48.57) * mm, v(1.78, 48.57) * mm, v(1.8, 48.57) * mm, v(1.83, 48.57) * mm, v(1.85, 48.57) * mm, v(1.86, 48.6) * mm, v(1.87, 48.66) * mm, v(1.85, 48.68) * mm, v(1.86, 48.72) * mm, v(1.87, 48.76) * mm, v(1.88, 48.78) * mm, v(1.9, 48.82) * mm, v(1.9, 48.86) * mm, v(1.91, 48.9) * mm, v(1.93, 48.96) * mm, v(1.93, 48.98) * mm, v(1.95, 49.03) * mm, v(1.96, 49.1) * mm, v(1.98, 49.13) * mm, v(1.98, 49.15) * mm, v(1.98, 49.16) * mm, v(1.98, 49.17) * mm, v(1.94, 49.17) * mm, v(1.92, 49.17) * mm, v(1.88, 49.18) * mm, v(1.85, 49.17) * mm, v(1.83, 49.17) * mm, v(1.82, 49.16) * mm, v(1.82, 49.13) * mm, v(1.81, 49.11) * mm, v(1.81, 49.1) * mm, v(1.8, 49.09) * mm, v(1.78, 49.08) * mm, v(1.75, 49.09) * mm, v(1.74, 49.09) * mm, v(1.72, 49.1) * mm, v(1.7, 49.1) * mm, v(1.7, 49.11) * mm, v(1.68, 49.14) * mm, v(1.67, 49.15) * mm, v(1.64, 49.16) * mm, v(1.62, 49.17) * mm, v(1.58, 49.18) * mm, v(1.56, 49.2) * mm, v(1.53, 49.21) * mm, v(1.5, 49.23) * mm, v(1.45, 49.22) * mm, v(1.4, 49.23) * mm, v(1.37, 49.23) * mm, v(1.33, 49.23) * mm, v(1.31, 49.23) * mm, v(1.28, 49.22) * mm, v(1.24, 49.2) * mm, v(1.23, 49.2) * mm], "startDerivative": vector(0.77, 4.8) * mm, "endDerivative": vector(-1.07, 0.44) * mm});
            skFitSpline(sketch, "E28", {"points": [v(1.22, 49.2) * mm, v(1.19, 49.2) * mm, v(1.18, 49.19) * mm], "startDerivative": vector(-0.05, 0) * mm, "endDerivative": vector(-0.02, -0.02) * mm});
            skFitSpline(sketch, "E29", {"points": [v(2.34, 48.44) * mm, v(2.26, 48.43) * mm, v(2.2, 48.4) * mm, v(2.16, 48.34) * mm, v(2.1, 48.3) * mm, v(2.07, 48.22) * mm, v(2.05, 48.16) * mm, v(2.03, 48.08) * mm, v(2.01, 48.03) * mm, v(1.97, 47.93) * mm, v(1.96, 47.87) * mm, v(1.95, 47.77) * mm, v(1.94, 47.71) * mm, v(1.94, 47.66) * mm, v(1.95, 47.61) * mm, v(1.96, 47.54) * mm, v(2, 47.5) * mm, v(2.03, 47.5) * mm, v(2.05, 47.49) * mm, v(2.1, 47.5) * mm, v(2.11, 47.5) * mm, v(2.15, 47.5) * mm, v(2.17, 47.52) * mm, v(2.19, 47.54) * mm, v(2.24, 47.58) * mm, v(2.27, 47.62) * mm, v(2.3, 47.64) * mm, v(2.31, 47.7) * mm, v(2.33, 47.72) * mm, v(2.36, 47.8) * mm, v(2.38, 47.84) * mm, v(2.4, 47.88) * mm, v(2.4, 47.9) * mm, v(2.4, 47.95) * mm, v(2.42, 48) * mm, v(2.43, 48.04) * mm, v(2.44, 48.07) * mm, v(2.44, 48.12) * mm, v(2.45, 48.18) * mm, v(2.45, 48.21) * mm, v(2.45, 48.24) * mm, v(2.45, 48.27) * mm, v(2.46, 48.3) * mm, v(2.45, 48.33) * mm, v(2.45, 48.35) * mm, v(2.44, 48.37) * mm, v(2.4, 48.39) * mm, v(2.4, 48.4) * mm, v(2.4, 48.41) * mm], "startDerivative": vector(-3.05, -0.13) * mm, "endDerivative": vector(-1.23, 0.78) * mm});
            skFitSpline(sketch, "E30", {"points": [v(2.34, 48.44) * mm, v(2.4, 48.41) * mm], "startDerivative": vector(0.06, -0.03) * mm, "endDerivative": vector(0.06, -0.03) * mm});
            skFitSpline(sketch, "E31", {"points": [v(3.62, 48.4) * mm, v(3.56, 48.4) * mm, v(3.54, 48.4) * mm, v(3.54, 48.4) * mm, v(3.52, 48.4) * mm, v(3.52, 48.4) * mm, v(3.5, 48.39) * mm, v(3.5, 48.38) * mm, v(3.48, 48.38) * mm, v(3.46, 48.36) * mm, v(3.45, 48.34) * mm, v(3.45, 48.33) * mm, v(3.44, 48.32) * mm, v(3.44, 48.3) * mm, v(3.43, 48.3) * mm, v(3.42, 48.28) * mm, v(3.42, 48.27) * mm, v(3.41, 48.26) * mm, v(3.4, 48.24) * mm, v(3.38, 48.16) * mm, v(3.35, 48.05) * mm, v(3.3, 47.93) * mm, v(3.27, 47.83) * mm, v(3.26, 47.76) * mm, v(3.25, 47.68) * mm, v(3.26, 47.6) * mm, v(3.28, 47.56) * mm, v(3.3, 47.54) * mm, v(3.33, 47.53) * mm, v(3.36, 47.52) * mm, v(3.39, 47.52) * mm, v(3.41, 47.52) * mm, v(3.48, 47.53) * mm, v(3.5, 47.54) * mm, v(3.53, 47.56) * mm, v(3.56, 47.6) * mm, v(3.57, 47.61) * mm, v(3.6, 47.66) * mm, v(3.63, 47.7) * mm, v(3.63, 47.72) * mm, v(3.64, 47.73) * mm, v(3.65, 47.77) * mm, v(3.66, 47.8) * mm, v(3.68, 47.83) * mm, v(3.7, 47.87) * mm, v(3.7, 47.91) * mm, v(3.7, 47.96) * mm, v(3.72, 47.99) * mm, v(3.73, 48.02) * mm, v(3.73, 48.07) * mm, v(3.75, 48.12) * mm, v(3.75, 48.18) * mm, v(3.75, 48.21) * mm, v(3.75, 48.28) * mm, v(3.75, 48.3) * mm, v(3.73, 48.33) * mm, v(3.72, 48.35) * mm, v(3.7, 48.37) * mm, v(3.68, 48.4) * mm, v(3.66, 48.4) * mm, v(3.62, 48.4) * mm]});
            skFitSpline(sketch, "E32", {"points": [v(6.15, 48.44) * mm, v(6.1, 48.44) * mm, v(6.08, 48.44) * mm, v(6.06, 48.41) * mm, v(6.04, 48.41) * mm, v(6, 48.39) * mm, v(5.99, 48.37) * mm, v(5.97, 48.33) * mm, v(5.96, 48.32) * mm, v(5.94, 48.3) * mm, v(5.92, 48.26) * mm, v(5.9, 48.22) * mm, v(5.9, 48.2) * mm, v(5.87, 48.15) * mm, v(5.86, 48.12) * mm, v(5.84, 48.05) * mm, v(5.83, 48) * mm, v(5.8, 47.93) * mm, v(5.77, 47.87) * mm, v(5.77, 47.82) * mm, v(5.77, 47.77) * mm, v(5.76, 47.75) * mm, v(5.76, 47.71) * mm, v(5.75, 47.68) * mm, v(5.75, 47.66) * mm, v(5.74, 47.63) * mm, v(5.74, 47.6) * mm, v(5.75, 47.58) * mm, v(5.76, 47.56) * mm, v(5.78, 47.54) * mm, v(5.8, 47.52) * mm, v(5.85, 47.51) * mm, v(5.89, 47.51) * mm, v(5.93, 47.5) * mm, v(5.98, 47.52) * mm, v(6, 47.53) * mm, v(6.05, 47.58) * mm, v(6.08, 47.6) * mm, v(6.13, 47.66) * mm, v(6.15, 47.72) * mm, v(6.16, 47.75) * mm, v(6.2, 47.8) * mm, v(6.2, 47.86) * mm, v(6.24, 47.93) * mm, v(6.24, 48) * mm, v(6.25, 48.05) * mm, v(6.25, 48.09) * mm, v(6.26, 48.14) * mm, v(6.27, 48.2) * mm, v(6.27, 48.24) * mm, v(6.27, 48.28) * mm, v(6.27, 48.33) * mm, v(6.26, 48.37) * mm, v(6.24, 48.39) * mm, v(6.23, 48.4) * mm, v(6.2, 48.41) * mm, v(6.15, 48.44) * mm]});
            skFitSpline(sketch, "E33", {"points": [v(6.34, 48.59) * mm, v(6.32, 48.6) * mm], "startDerivative": vector(-0.01, 0) * mm, "endDerivative": vector(-0.01, 0) * mm});
            skFitSpline(sketch, "E34", {"points": [v(1.23, 49.2) * mm, v(1.22, 49.2) * mm], "startDerivative": vector(-0.01, 0) * mm, "endDerivative": vector(-0.01, 0) * mm});
            skSolve(sketch);
        }
        {
            var Q0;
            {var subQ0=sQuery(id+"F6.wireOp",EDGE,"E18");Q0=makeQuery(id+"F6.imprint","IMPRINT",FACE,{"disambiguationData":[TD([[makeQuery(id+"F6.imprint","IMPRINT",EDGE,{"derivedFrom":subQ0}),1.0]])]});}
            var Q1;
            Q1=makeQuery(id+"F6.imprint","IMPRINT",FACE,{"disambiguationData":[TD([[makeQuery(id+"F6.imprint","IMPRINT",EDGE,{"derivedFrom":sQuery(id+"F6.wireOp",EDGE,"E24")}),1.0]])]});
            extrude(context, id + "F7", {"entities" : qUnion([Q0, Q1]), "operationType" : NewBodyOperationType.REMOVE, "oppositeDirection" : true, "depth" : 0.1 * mm, "offsetDistance" : 25 * mm});
        }
        {
            var Q0;
            {var subQ0=sQuery(id+"F0.wireOp",EDGE,"E0.top");var subQ1=sQuery(id+"F0.wireOp",EDGE,"E0.left");var subQ2=sQuery(id+"F0.wireOp",EDGE,"E0.right");Q0=makeQuery(id+"F5.boolean.opBoolean","SPLIT",FACE,{"disambiguationData":[TD([makeQuery(id+"F1.opExtrude","SWEPT_FACE",FACE,{"disambiguationData":[OSD([subQ0])]})])],"derivedFrom":makeQuery(id+"F1.opExtrude","CAP_FACE",FACE,{"disambiguationData":[OSD([sQuery(id+"F0.wireOp",EDGE,"E0.bottom"),subQ0,subQ1,subQ2])],"isStart":false})});}
            var sketch = newSketch(context, id + "F8", { "sketchPlane" : qUnion([Q0])});
            skLineSegment(sketch, "E35", {"start": v(4.72, -16.52) * mm, "end": v(4.72, -10.52) * mm});
            skLineSegment(sketch, "E36", {"start": v(4.72, -10.52) * mm, "end": v(3.52, -10.52) * mm});
            skLineSegment(sketch, "E37", {"start": v(3.52, -10.52) * mm, "end": v(3.52, -16.52) * mm});
            skLineSegment(sketch, "E38", {"start": v(3.52, -16.52) * mm, "end": v(4.72, -16.52) * mm});
            skLineSegment(sketch, "E39", {"start": v(-4.48, -16.52) * mm, "end": v(-4.48, -10.52) * mm});
            skLineSegment(sketch, "E40", {"start": v(-4.48, -10.52) * mm, "end": v(-3.28, -10.52) * mm});
            skLineSegment(sketch, "E41", {"start": v(-3.28, -16.52) * mm, "end": v(-4.48, -16.52) * mm});
            skLineSegment(sketch, "E42", {"start": v(-3.28, -10.52) * mm, "end": v(-3.28, -16.52) * mm});
            skSolve(sketch);
        }
        {
            var Q0;
            Q0=makeQuery(id+"F8.imprint","IMPRINT",FACE,{"disambiguationData":[TD([[makeQuery(id+"F8.imprint","IMPRINT",EDGE,{"derivedFrom":sQuery(id+"F8.wireOp",EDGE,"E39")}),-1.0]])]});
            var Q1;
            Q1=makeQuery(id+"F8.imprint","IMPRINT",FACE,{"disambiguationData":[TD([[makeQuery(id+"F8.imprint","IMPRINT",EDGE,{"derivedFrom":sQuery(id+"F8.wireOp",EDGE,"E35")}),1.0]])]});
            extrude(context, id + "F9", {"entities" : qUnion([Q0, Q1]), "operationType" : NewBodyOperationType.REMOVE, "oppositeDirection" : true, "depth" : 0.2 * mm, "offsetDistance" : 25 * mm});
        }
        {
            var Q0;
            {var subQ0=sQuery(id+"F0.wireOp",EDGE,"E0.top");var subQ1=sQuery(id+"F0.wireOp",EDGE,"E0.left");var subQ2=sQuery(id+"F0.wireOp",EDGE,"E0.right");Q0=makeQuery(id+"F5.boolean.opBoolean","SPLIT",FACE,{"disambiguationData":[TD([makeQuery(id+"F1.opExtrude","SWEPT_FACE",FACE,{"disambiguationData":[OSD([subQ0])]})])],"derivedFrom":makeQuery(id+"F1.opExtrude","CAP_FACE",FACE,{"disambiguationData":[OSD([sQuery(id+"F0.wireOp",EDGE,"E0.bottom"),subQ0,subQ1,subQ2])],"isStart":false})});}
            var sketch = newSketch(context, id + "F10", { "sketchPlane" : qUnion([Q0])});
            skLineSegment(sketch, "E43", {"start": v(4.12, -6.52) * mm, "end": v(4.12, 9.68) * mm});
            skLineSegment(sketch, "E44", {"start": v(4.12, 9.68) * mm, "end": v(-3.88, 9.68) * mm});
            skLineSegment(sketch, "E45", {"start": v(4.12, -6.52) * mm, "end": v(-3.88, -6.52) * mm});
            skLineSegment(sketch, "E46", {"start": v(-3.88, -6.52) * mm, "end": v(-3.88, 9.68) * mm});
            skSolve(sketch);
        }
        {
            var Q0;
            Q0=makeQuery(id+"F10.imprint","IMPRINT",FACE,{"disambiguationData":[TD([[makeQuery(id+"F10.imprint","IMPRINT",EDGE,{"derivedFrom":sQuery(id+"F10.wireOp",EDGE,"E43")}),1.0]])]});
            extrude(context, id + "F11", {"entities" : qUnion([Q0]), "operationType" : NewBodyOperationType.REMOVE, "oppositeDirection" : true, "depth" : 0.1 * mm, "offsetDistance" : 25 * mm});
        }
        {
            var Q0;
            Q0=makeQuery(id+"F11.boolean.opBoolean","COPY",FACE,{"derivedFrom":makeQuery(id+"F11.opExtrude","CAP_FACE",FACE,{"disambiguationData":[OSD([sQuery(id+"F10.wireOp",EDGE,"E43"),sQuery(id+"F10.wireOp",EDGE,"E44"),sQuery(id+"F10.wireOp",EDGE,"E45"),sQuery(id+"F10.wireOp",EDGE,"E46")])],"isStart":false})});
            var sketch = newSketch(context, id + "F12", { "sketchPlane" : qUnion([Q0])});
            skCircle(sketch, "E47", {"center": v(0.12, -4.02) * mm, "radius": 1.1 * mm});
            skCircle(sketch, "E48", {"center": v(0.12, -0.82) * mm, "radius": 1.1 * mm});
            skCircle(sketch, "E49", {"center": v(0.12, 3.98) * mm, "radius": 1.1 * mm});
            skCircle(sketch, "E50", {"center": v(0.12, 7.18) * mm, "radius": 1.1 * mm});
            skSolve(sketch);
        }
        {
            var Q0;
            Q0=makeQuery(id+"F12.imprint","IMPRINT",FACE,{"disambiguationData":[TD([[makeQuery(id+"F12.imprint","IMPRINT",EDGE,{"derivedFrom":sQuery(id+"F12.wireOp",EDGE,"E50")}),1.0]])]});
            var Q1;
            Q1=makeQuery(id+"F12.imprint","IMPRINT",FACE,{"disambiguationData":[TD([[makeQuery(id+"F12.imprint","IMPRINT",EDGE,{"derivedFrom":sQuery(id+"F12.wireOp",EDGE,"E49")}),1.0]])]});
            var Q2;
            Q2=makeQuery(id+"F12.imprint","IMPRINT",FACE,{"disambiguationData":[TD([[makeQuery(id+"F12.imprint","IMPRINT",EDGE,{"derivedFrom":sQuery(id+"F12.wireOp",EDGE,"E48")}),1.0]])]});
            var Q3;
            Q3=makeQuery(id+"F12.imprint","IMPRINT",FACE,{"disambiguationData":[TD([[makeQuery(id+"F12.imprint","IMPRINT",EDGE,{"derivedFrom":sQuery(id+"F12.wireOp",EDGE,"E47")}),1.0]])]});
            extrude(context, id + "F13", {"entities" : qUnion([Q0, Q1, Q2, Q3]), "operationType" : NewBodyOperationType.REMOVE, "oppositeDirection" : true, "depth" : 0.1 * mm, "offsetDistance" : 25 * mm});
        }
    });
